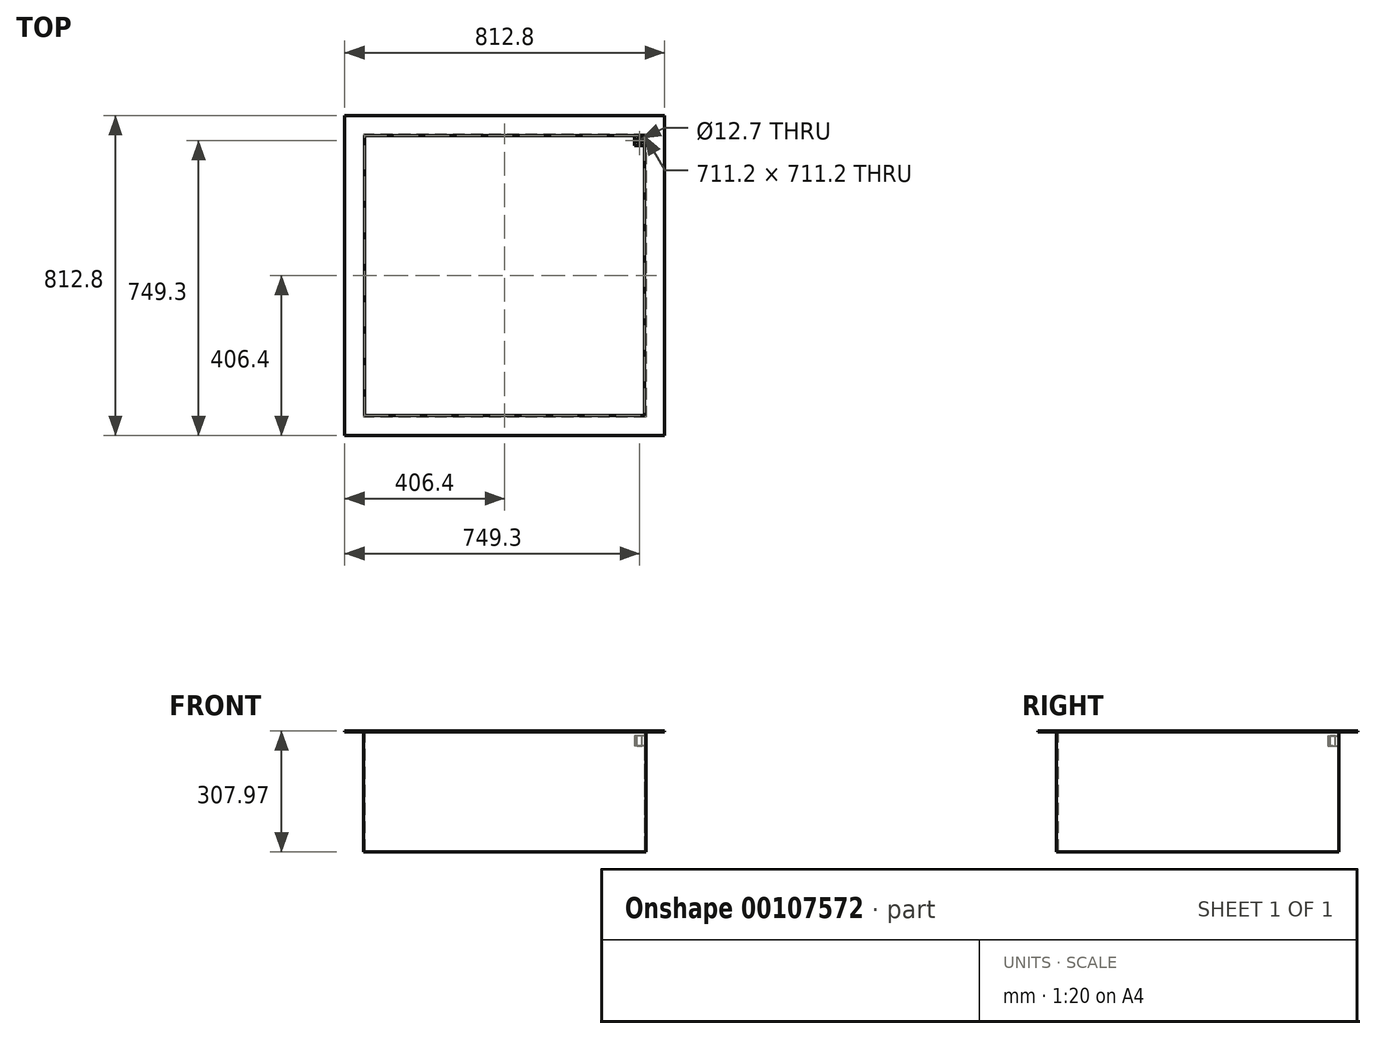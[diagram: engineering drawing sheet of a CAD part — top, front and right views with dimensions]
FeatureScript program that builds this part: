
annotation { "Feature Type Name" : "Feature", "Feature Type Description" : "" }
export const myFeature = defineFeature(function(context is Context, id is Id, definition is map)
    precondition{}
    {
        {
            var Q0;
            Q0=qCreatedBy(makeId("Top.planeOp"),FACE);
            var sketch = newSketch(context, id + "F0", { "sketchPlane" : qUnion([Q0])});
            skLineSegment(sketch, "E0.bottom", {"start": v(406.4, -406.4) * mm, "end": v(-406.4, -406.4) * mm});
            skLineSegment(sketch, "E0.top", {"start": v(406.4, 406.4) * mm, "end": v(-406.4, 406.4) * mm});
            skLineSegment(sketch, "E0.left", {"start": v(406.4, -406.4) * mm, "end": v(406.4, 406.4) * mm});
            skLineSegment(sketch, "E0.right", {"start": v(-406.4, -406.4) * mm, "end": v(-406.4, 406.4) * mm});
            skPoint(sketch, "E0.middle", {"position": v(0, 0) * mm});
            skLineSegment(sketch, "E1.0", {"start": v(355.6, 355.6) * mm, "end": v(-355.6, 355.6) * mm});
            skLineSegment(sketch, "E1.1", {"start": v(355.6, -355.6) * mm, "end": v(355.6, 355.6) * mm});
            skLineSegment(sketch, "E1.2", {"start": v(355.6, -355.6) * mm, "end": v(-355.6, -355.6) * mm});
            skLineSegment(sketch, "E1.3", {"start": v(-355.6, -355.6) * mm, "end": v(-355.6, 355.6) * mm});
            skSolve(sketch);
        }
        {
            var Q0;
            Q0 = qSketchRegion(id + "F0", true);
            extrude(context, id + "F1", {"entities" : qUnion([Q0]), "depth" : 3.17 * mm});
        }
        {
            var Q0;
            Q0=makeQuery(id+"F1.opExtrude","CAP_FACE",FACE,{"disambiguationData":[OSD([sQuery(id+"F0.wireOp",EDGE,"E0.bottom"),sQuery(id+"F0.wireOp",EDGE,"E0.top"),sQuery(id+"F0.wireOp",EDGE,"E0.left"),sQuery(id+"F0.wireOp",EDGE,"E0.right"),sQuery(id+"F0.wireOp",EDGE,"E1.0"),sQuery(id+"F0.wireOp",EDGE,"E1.1"),sQuery(id+"F0.wireOp",EDGE,"E1.2"),sQuery(id+"F0.wireOp",EDGE,"E1.3")])],"isStart":true});
            var sketch = newSketch(context, id + "F2", { "sketchPlane" : qUnion([Q0])});
            skLineSegment(sketch, "E2.bottom", {"start": v(355.6, -355.6) * mm, "end": v(-355.6, -355.6) * mm});
            skLineSegment(sketch, "E2.top", {"start": v(355.6, 355.6) * mm, "end": v(-355.6, 355.6) * mm});
            skLineSegment(sketch, "E2.left", {"start": v(355.6, -355.6) * mm, "end": v(355.6, 355.6) * mm});
            skLineSegment(sketch, "E2.right", {"start": v(-355.6, -355.6) * mm, "end": v(-355.6, 355.6) * mm});
            skPoint(sketch, "E2.middle", {"position": v(0, 0) * mm});
            skLineSegment(sketch, "E3.0", {"start": v(358.78, 358.78) * mm, "end": v(-358.78, 358.78) * mm});
            skLineSegment(sketch, "E3.1", {"start": v(358.78, -358.78) * mm, "end": v(358.78, 358.78) * mm});
            skLineSegment(sketch, "E3.2", {"start": v(358.78, -358.78) * mm, "end": v(-358.78, -358.78) * mm});
            skLineSegment(sketch, "E3.3", {"start": v(-358.78, -358.78) * mm, "end": v(-358.78, 358.78) * mm});
            skSolve(sketch);
        }
        {
            var Q0;
            Q0 = qSketchRegion(id + "F2", true);
            extrude(context, id + "F3", {"entities" : qUnion([Q0]), "operationType" : NewBodyOperationType.ADD, "depth" : 304.8 * mm});
        }
        {
            var Q0;
            Q0=makeQuery(id+"F3.boolean.opBoolean","MERGE",FACE,{"derivedFrom":[makeQuery(id+"F1.opExtrude","SWEPT_FACE",FACE,{"disambiguationData":[OSD([sQuery(id+"F0.wireOp",EDGE,"E1.0")])]}),makeQuery(id+"F3.opExtrude","SWEPT_FACE",FACE,{"disambiguationData":[OSD([sQuery(id+"F2.wireOp",EDGE,"E2.bottom")])]})]});
            var sketch = newSketch(context, id + "F4", { "sketchPlane" : qUnion([Q0])});
            skLineSegment(sketch, "E4.bottom", {"start": v(355.6, -9.52) * mm, "end": v(330.2, -9.53) * mm});
            skLineSegment(sketch, "E4.top", {"start": v(355.6, -34.93) * mm, "end": v(330.2, -34.93) * mm});
            skLineSegment(sketch, "E4.left", {"start": v(355.6, -9.52) * mm, "end": v(355.6, -34.93) * mm});
            skLineSegment(sketch, "E4.right", {"start": v(330.2, -9.53) * mm, "end": v(330.2, -34.92) * mm});
            skSolve(sketch);
        }
        {
            var Q0;
            Q0 = qSketchRegion(id + "F4", true);
            extrude(context, id + "F5", {"entities" : qUnion([Q0]), "operationType" : NewBodyOperationType.ADD, "depth" : 25.4 * mm});
        }
        {
            var Q0;
            Q0=makeQuery(id+"F5.opExtrude","SWEPT_FACE",FACE,{"disambiguationData":[OSD([sQuery(id+"F4.wireOp",EDGE,"E4.bottom")])]});
            var sketch = newSketch(context, id + "F6", { "sketchPlane" : qUnion([Q0])});
            skCircle(sketch, "E5", {"center": v(342.9, 342.9) * mm, "radius": 6.35 * mm});
            skSolve(sketch);
        }
        {
            var Q0;
            Q0 = qSketchRegion(id + "F6", true);
            var Q1;
            Q1=makeQuery(id+"F5.opExtrude","SWEPT_FACE",FACE,{"disambiguationData":[OSD([sQuery(id+"F4.wireOp",EDGE,"E4.top")])]});
            extrude(context, id + "F7", {"entities" : qUnion([Q0]), "operationType" : NewBodyOperationType.REMOVE, "endBound" : BoundingType.UP_TO_SURFACE, "oppositeDirection" : true, "endBoundEntityFace" : qUnion([Q1]), "depth" : 25.4 * mm});
        }
    });
